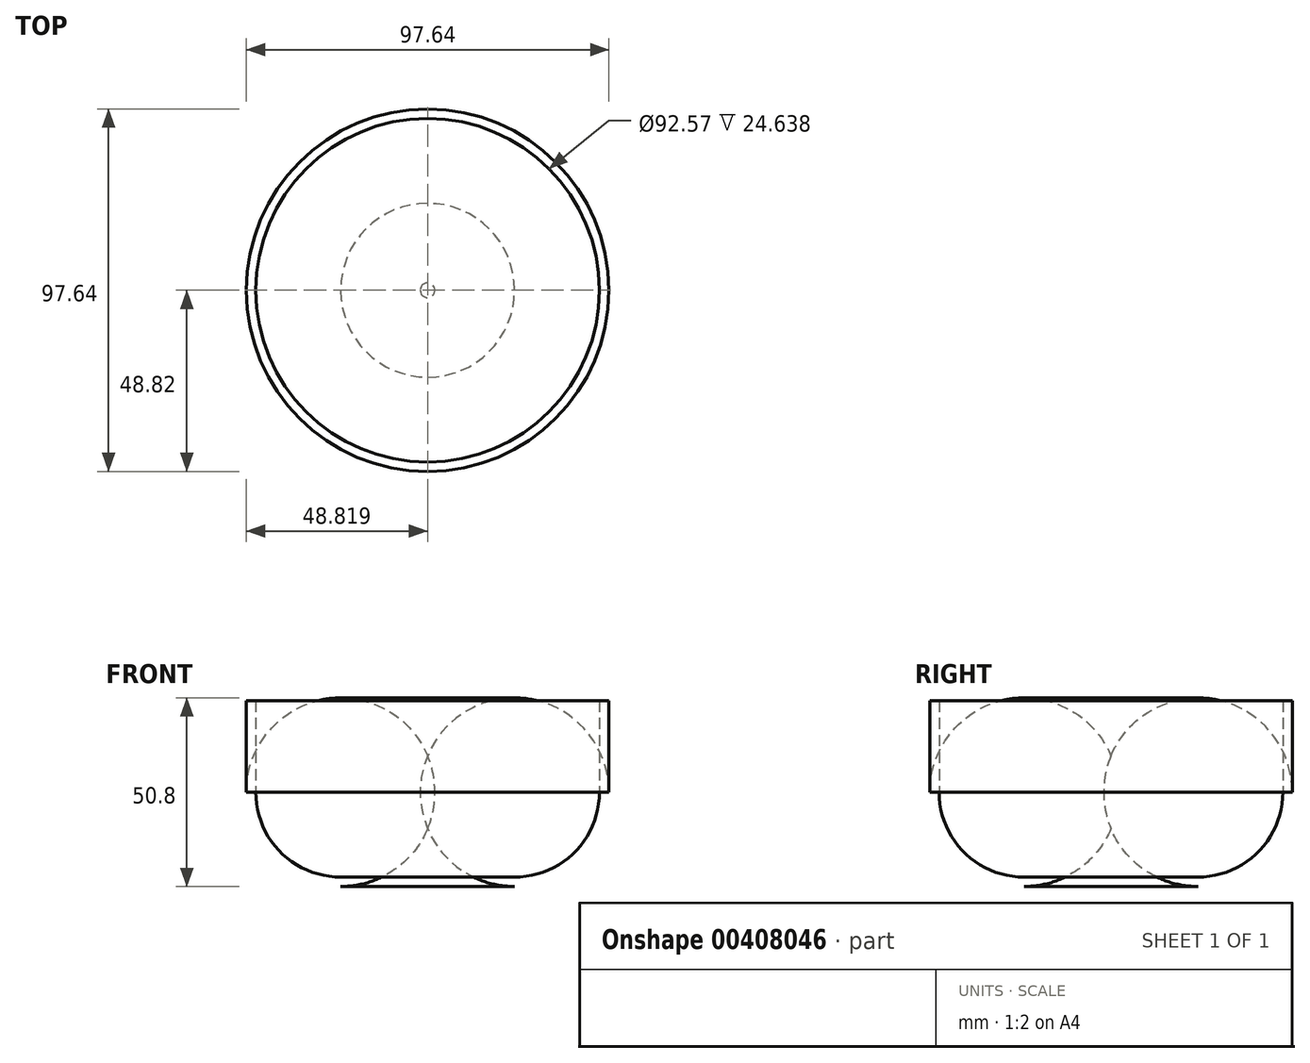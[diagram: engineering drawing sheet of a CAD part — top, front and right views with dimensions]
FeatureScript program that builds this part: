
annotation { "Feature Type Name" : "Feature", "Feature Type Description" : "" }
export const myFeature = defineFeature(function(context is Context, id is Id, definition is map)
    precondition{}
    {
        {
            var Q0;
            Q0=qCreatedBy(makeId("Top.planeOp"),FACE);
            var sketch = newSketch(context, id + "F0", { "sketchPlane" : qUnion([Q0])});
            skLineSegment(sketch, "E0", {"start": v(0, 0) * mm, "end": v(0, 0) * mm});
            skCircle(sketch, "E1", {"center": v(-40.95, 14.97) * mm, "radius": 48.82 * mm});
            skSolve(sketch);
        }
        {
            var Q0;
            Q0 = qSketchRegion(id + "F0", true);
            extrude(context, id + "F1", {"entities" : qUnion([Q0]), "depth" : 50.04 * mm});
        }
        {
            var Q0;
            Q0=makeQuery(id+"F1.opExtrude","CAP_EDGE",EDGE,{"disambiguationData":[OSD([sQuery(id+"F0.wireOp",EDGE,"E1")])],"isStart":true});
            fillet(context, id + "F2", {"entities" : qUnion([Q0]), "radius" : 25.4 * mm, "tangentPropagation" : true, "allowEdgeOverflow" : false});
        }
        {
            var Q0;
            Q0=makeQuery(id+"F1.opExtrude","CAP_FACE",FACE,{"disambiguationData":[OSD([sQuery(id+"F0.wireOp",EDGE,"E1")])],"isStart":false});
            shell(context, id + "F3", {"entities" : qUnion([Q0]), "thickness" : 2.54 * mm});
        }
    });
